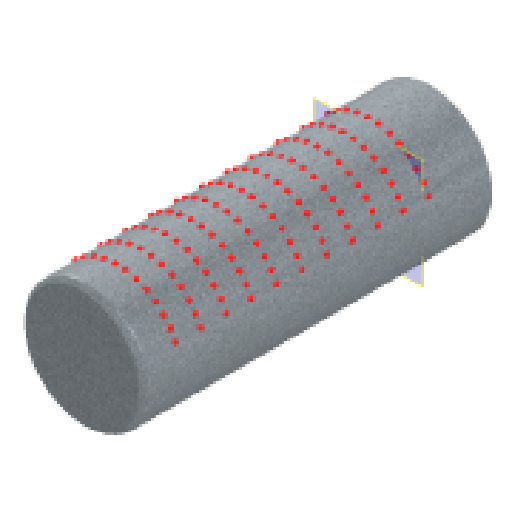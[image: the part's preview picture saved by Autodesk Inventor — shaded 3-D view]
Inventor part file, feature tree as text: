
AUTODESK INVENTOR PART (.ipt)
format: ipt  version: 2023 (Build 270158000, 158)  size: 679,424 bytes
history: native  units: in
note: dims shown in document units (in); Inventor stores cm internally (conversion verified against a paired STEP export)
features: extrude x2, fillet x2, sketch x2, chamfer x1, plane x1, pattern_linear x1
ambient origin geometry x8: Origin, YZ Plane, XZ Plane, XY Plane, X Axis, Y Axis, Z Axis, Center Point
bodies: Solid1 (feature_tree)
feature tree (9):
  extrude  "Extrusion1"  Depth=137.7953in TaperAngle=0.0deg
  chamfer  "Chamfer1"  Distance=2.0in Angle=45.0deg
  fillet  "Fillet1"  Radius=2.0in
  plane  "Work Plane1"
  extrude  "Extrusion2"  Depth=1.0in
  fillet  "Fillet2"  Radius=2.0in
  pattern_linear  "Rectangular Pattern1"  Spacing1=2.0in  [1 undecoded]
  sketch  "Sketch1"  dims[d0=78.7402in d1=137.7953in d2=0.0in d3=2.0in d4=0.125in d5=45.0deg d6=2.0in]
  sketch  "Sketch2"  dims[d7=-24.4375in d8=4.7244in d10=0.7559in d12=2.0in d13=2.0in d14=0.0in d15=1.0in d16=4.3307in d18=10.0in]
note: 1 required parameter value undecoded (feature->parameter linkage not recoverable at this tier; creation-order binding heuristic only, values carry confidence <= 0.55)
